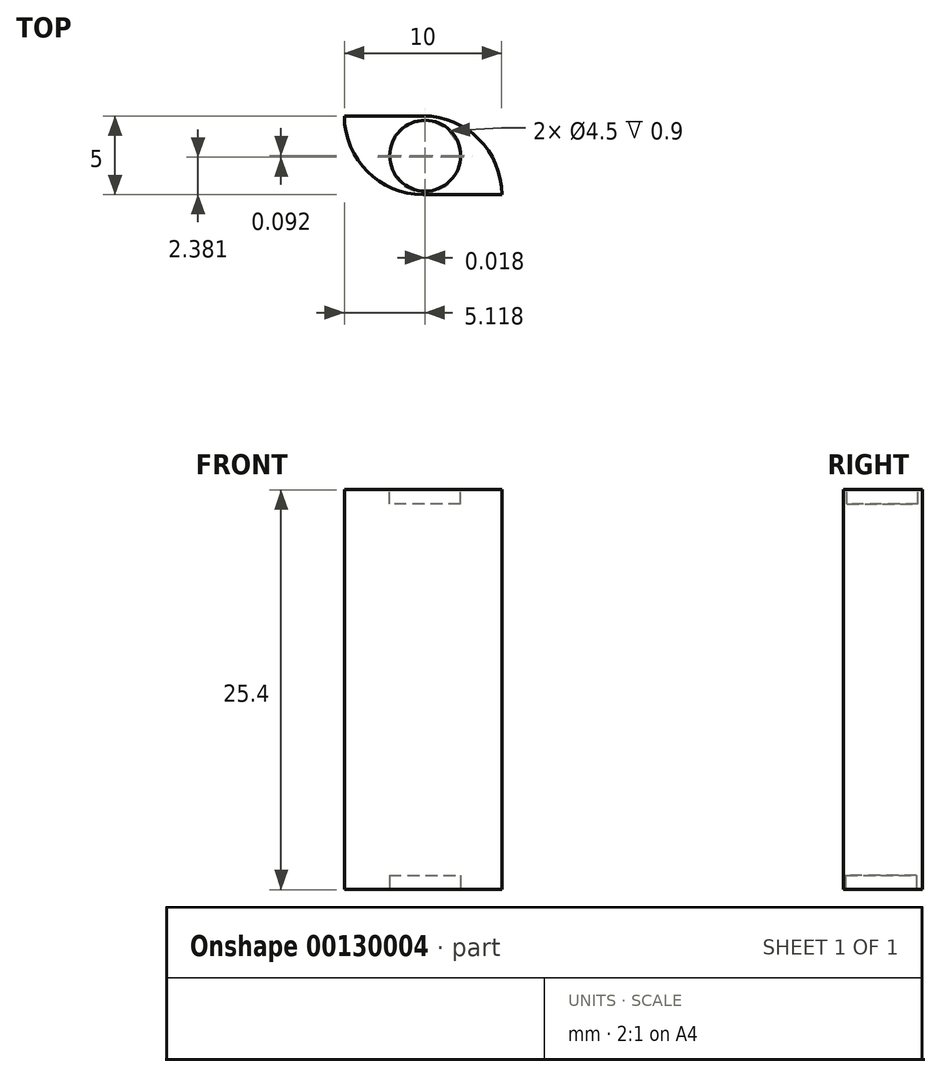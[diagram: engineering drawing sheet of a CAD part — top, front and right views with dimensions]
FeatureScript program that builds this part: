
annotation { "Feature Type Name" : "Feature", "Feature Type Description" : "" }
export const myFeature = defineFeature(function(context is Context, id is Id, definition is map)
    precondition{}
    {
        {
            var Q0;
            Q0=qCreatedBy(makeId("Front.planeOp"),FACE);
            var sketch = newSketch(context, id + "F0", { "sketchPlane" : qUnion([Q0])});
            skLineSegment(sketch, "E0.bottom", {"start": v(-8.64, 12.1) * mm, "end": v(1.36, 12.1) * mm});
            skLineSegment(sketch, "E0.top", {"start": v(-8.64, -13.3) * mm, "end": v(1.36, -13.3) * mm});
            skLineSegment(sketch, "E0.left", {"start": v(-8.64, 12.1) * mm, "end": v(-8.64, -13.3) * mm});
            skLineSegment(sketch, "E0.right", {"start": v(1.36, 12.1) * mm, "end": v(1.36, -13.3) * mm});
            skSolve(sketch);
        }
        {
            var Q0;
            Q0 = qSketchRegion(id + "F0", true);
            extrude(context, id + "F1", {"entities" : qUnion([Q0]), "depth" : 5 * mm});
        }
        {
            var Q0;
            Q0=makeQuery(id+"F1.opExtrude","CAP_EDGE",EDGE,{"disambiguationData":[OSD([sQuery(id+"F0.wireOp",EDGE,"E0.right")])],"isStart":true});
            var Q1;
            Q1=makeQuery(id+"F1.opExtrude","CAP_EDGE",EDGE,{"disambiguationData":[OSD([sQuery(id+"F0.wireOp",EDGE,"E0.left")])],"isStart":false});
            fillet(context, id + "F2", {"entities" : qUnion([Q0, Q1]), "radius" : 5 * mm, "tangentPropagation" : true, "allowEdgeOverflow" : false});
        }
        {
            var Q0;
            Q0=makeQuery(id+"F1.opExtrude","SWEPT_FACE",FACE,{"disambiguationData":[OSD([sQuery(id+"F0.wireOp",EDGE,"E0.bottom")])]});
            var sketch = newSketch(context, id + "F3", { "sketchPlane" : qUnion([Q0])});
            skCircle(sketch, "E1", {"center": v(-3.5, -2.53) * mm, "radius": 2.25 * mm});
            skSolve(sketch);
        }
        {
            var Q0;
            {var subQ0=sQuery(id+"F3.wireOp",EDGE,"E1");var subQ1=makeQuery(id+"F2.opFillet","BLEND_EDGE",EDGE,{"blendedFrom":[makeQuery(id+"F1.opExtrude","CAP_EDGE",EDGE,{"disambiguationData":[OSD([sQuery(id+"F0.wireOp",EDGE,"E0.right")])],"isStart":true}),makeQuery(id+"F1.opExtrude","SWEPT_FACE",FACE,{"disambiguationData":[OSD([sQuery(id+"F0.wireOp",EDGE,"E0.bottom")])]})],"blendedInto":[makeQuery(id+"F1.opExtrude","SWEPT_FACE",FACE,{"disambiguationData":[OSD([sQuery(id+"F0.wireOp",EDGE,"E0.bottom")])]})]});var subQ2=makeQuery(id+"F3.imprint","INTERSECT",VERTEX,{"disambiguationData":[OD(0.0)],"derivedFrom":[subQ1,subQ0]});Q0=makeQuery(id+"F3.imprint","IMPRINT",FACE,{"disambiguationData":[TD([[makeQuery(id+"F3.imprint","IMPRINT",EDGE,{"disambiguationData":[TD([[subQ2,-1.0]])],"derivedFrom":subQ0}),1.0]])]});}
            extrude(context, id + "F4", {"entities" : qUnion([Q0]), "operationType" : NewBodyOperationType.REMOVE, "oppositeDirection" : true, "depth" : 0.9 * mm});
        }
        {
            var Q0;
            Q0=makeQuery(id+"F1.opExtrude","SWEPT_FACE",FACE,{"disambiguationData":[OSD([sQuery(id+"F0.wireOp",EDGE,"E0.top")])]});
            var sketch = newSketch(context, id + "F5", { "sketchPlane" : qUnion([Q0])});
            skCircle(sketch, "E2", {"center": v(-3.52, 2.62) * mm, "radius": 2.25 * mm});
            skSolve(sketch);
        }
        {
            var Q0;
            Q0=makeQuery(id+"F5.imprint","IMPRINT",FACE,{"disambiguationData":[TD([[makeQuery(id+"F5.imprint","IMPRINT",EDGE,{"derivedFrom":sQuery(id+"F5.wireOp",EDGE,"E2")}),1.0]])]});
            extrude(context, id + "F6", {"entities" : qUnion([Q0]), "operationType" : NewBodyOperationType.REMOVE, "oppositeDirection" : true, "depth" : 0.9 * mm});
        }
    });
